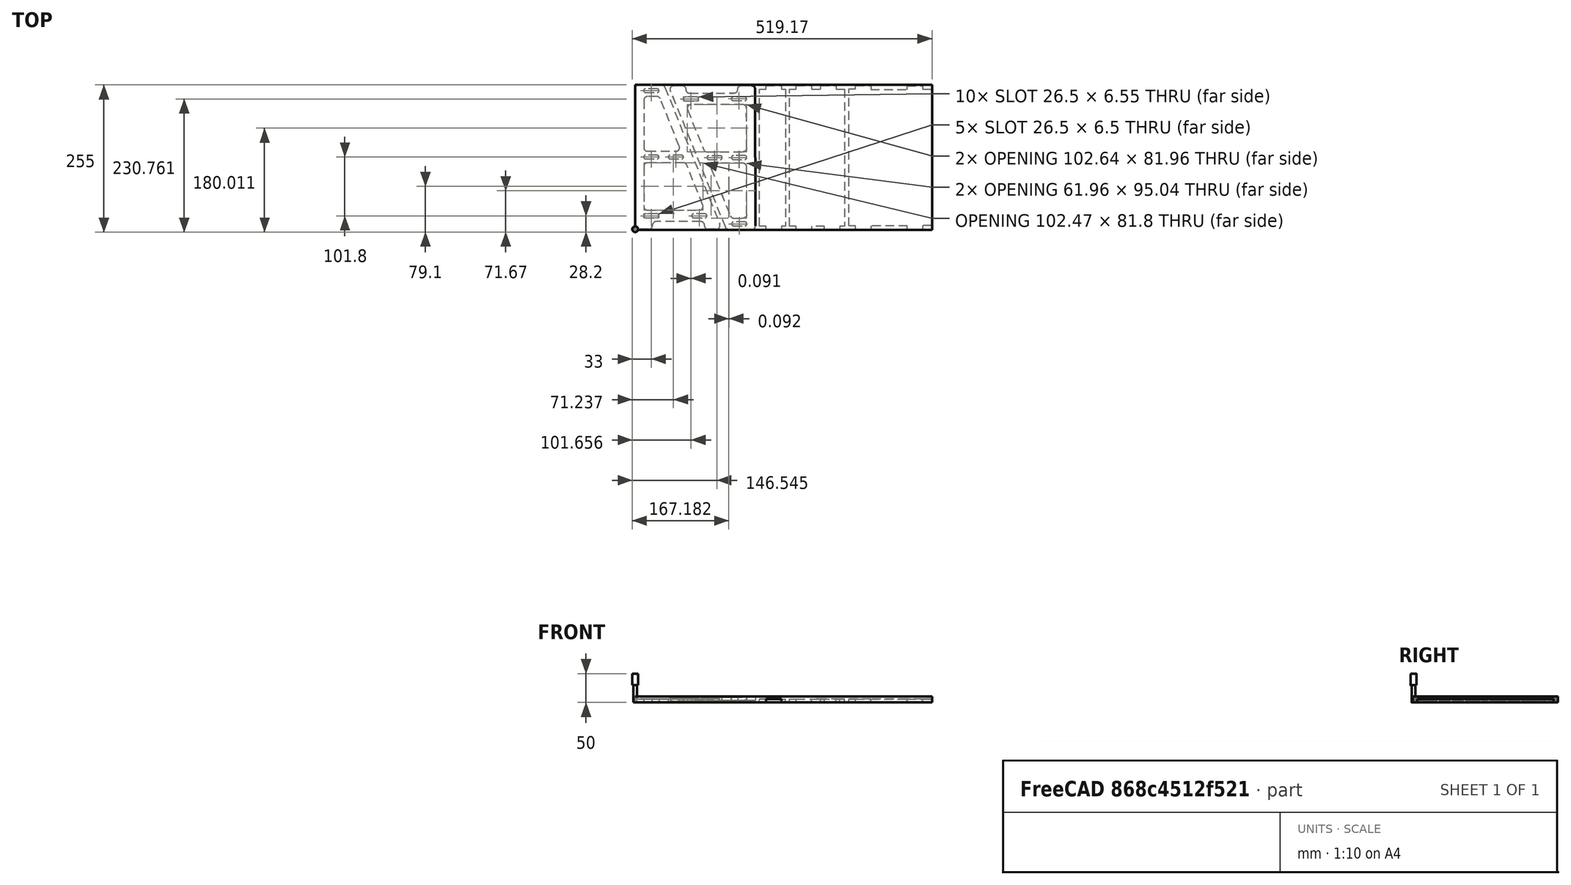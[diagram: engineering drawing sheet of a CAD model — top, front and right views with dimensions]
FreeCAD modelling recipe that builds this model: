
FCSTD DOCUMENT  (FreeCAD 0.19R14555 (Git shallow))
Label: Stand2
License: All rights reserved
LicenseURL: http://en.wikipedia.org/wiki/All_rights_reserved
objects: Part::FeaturePython×8, Sketcher::SketchObject×4, PartDesign::Pad×4, PartDesign::Body×4, Path::FeaturePython×4, App::DocumentObjectGroup×2, PartDesign::Fillet×1, App::FeaturePython×1, Spreadsheet::Sheet×1, Part::Mirroring×1, Path::FeatureCompoundPython×1, Mesh::FeaturePython×1
note: 29 computed .brp shape members not serialized (recipe doc carries the construction recipe); baked Part::Feature solids carry a one-line shape summary decoded from their .brp

FEATURE [Sketcher::SketchObject] Sketch
  FullyConstrained = true
  MapMode = 5
  Support = -> [XY_Plane]
  expr: Constraints[96] = <<Spreadsheet>>.TongueGapLower
  expr: Constraints[94] = <<Spreadsheet>>.SlotCentre
  expr: Constraints[83] = <<Spreadsheet>>.TongueToBack
  expr: Constraints[81] = <<Spreadsheet>>.Tool
  expr: Constraints[72] = <<Spreadsheet>>.TongueToBack
  expr: Constraints[91] = <<Spreadsheet>>.SlotSize
  expr: Constraints[92] = <<Spreadsheet>>.Tool
  expr: Constraints[71] = <<Spreadsheet>>.SlotSize
  expr: Constraints[67] = <<Spreadsheet>>.Tool
  expr: Constraints[53] = <<Spreadsheet>>.Tool
  expr: Constraints[68] = <<Spreadsheet>>.Tool
  expr: Constraints[82] = <<Spreadsheet>>.SlotSize
  expr: Constraints[52] = <<Spreadsheet>>.SlotSize
  expr: Constraints[27] = <<Spreadsheet>>.Top
  expr: Constraints[70] = <<Spreadsheet>>.SlotSize
  expr: Constraints[55] = <<Spreadsheet>>.TongueToBack
  expr: Constraints[29] = <<Spreadsheet>>.Bottom
  expr: Constraints[95] = <<Spreadsheet>>.TongueGapMid
  expr: Constraints[26] = <<Spreadsheet>>.Height
  sketch-geometry (36):
    g0: LineSegment StartX=0 StartY=250 StartZ=0 EndX=50 EndY=250 EndZ=0
    g1: LineSegment StartX=150 StartY=0 StartZ=0 EndX=120 EndY=0 EndZ=0
    g2: LineSegment StartX=0 StartY=0 StartZ=0 EndX=0 EndY=250 EndZ=0
    g3: LineSegment StartX=50 StartY=250 StartZ=0 EndX=150 EndY=0 EndZ=0
    g4: LineSegment StartX=15 StartY=230 StartZ=0 EndX=15 EndY=135 EndZ=0
    g5: LineSegment StartX=15 StartY=135 StartZ=0 EndX=79.8445 EndY=135 EndZ=0
    g6: LineSegment StartX=79.8445 StartY=135 StartZ=0 EndX=41.8445 EndY=230 EndZ=0
    g7: LineSegment StartX=41.8445 StartY=230 StartZ=0 EndX=15 EndY=230 EndZ=0
    g8: LineSegment StartX=15 StartY=115 StartZ=0 EndX=15 EndY=33.2 EndZ=0
    g9: LineSegment StartX=15 StartY=33.2 StartZ=0 EndX=120.565 EndY=33.2 EndZ=0
    g10: LineSegment StartX=120.565 StartY=33.2 StartZ=0 EndX=87.8445 EndY=115 EndZ=0
    g11: LineSegment StartX=87.8445 StartY=115 StartZ=0 EndX=15 EndY=115 EndZ=0
    g12: LineSegment StartX=120 StartY=0 StartZ=0 EndX=120 EndY=13.2 EndZ=0
    g13: LineSegment StartX=120 StartY=13.2 StartZ=0 EndX=30 EndY=13.2 EndZ=0
    g14: LineSegment StartX=30 StartY=13.2 StartZ=0 EndX=30 EndY=0 EndZ=0
    g15: LineSegment StartX=30 StartY=0 StartZ=0 EndX=0 EndY=0 EndZ=0
    g16: ArcOfCircle CenterX=18 CenterY=240 CenterZ=0 NormalX=0 NormalY=0 NormalZ=1 AngleXU=0 Radius=3.25 StartAngle=1.5708 EndAngle=4.71239
    g17: ArcOfCircle CenterX=38 CenterY=240 CenterZ=0 NormalX=0 NormalY=0 NormalZ=1 AngleXU=0 Radius=3.25 StartAngle=4.71239 EndAngle=7.85398
    g18: LineSegment StartX=18 StartY=236.75 StartZ=0 EndX=38 EndY=236.75 EndZ=0
    g19: LineSegment StartX=38 StartY=243.25 StartZ=0 EndX=18 EndY=243.25 EndZ=0
    g20: ArcOfCircle CenterX=60.5 CenterY=125 CenterZ=0 NormalX=0 NormalY=0 NormalZ=1 AngleXU=0 Radius=3.25 StartAngle=1.5708 EndAngle=4.71239
    g21: ArcOfCircle CenterX=80.5 CenterY=125 CenterZ=0 NormalX=0 NormalY=0 NormalZ=1 AngleXU=0 Radius=3.25 StartAngle=4.71239 EndAngle=7.85398
    g22: LineSegment StartX=60.5 StartY=121.75 StartZ=0 EndX=80.5 EndY=121.75 EndZ=0
    g23: LineSegment StartX=80.5 StartY=128.25 StartZ=0 EndX=60.5 EndY=128.25 EndZ=0
    g24: ArcOfCircle CenterX=18 CenterY=125 CenterZ=0 NormalX=0 NormalY=0 NormalZ=1 AngleXU=0 Radius=3.25 StartAngle=1.5708 EndAngle=4.71239
    g25: ArcOfCircle CenterX=38 CenterY=125 CenterZ=0 NormalX=0 NormalY=0 NormalZ=1 AngleXU=0 Radius=3.25 StartAngle=4.71239 EndAngle=7.85398
    g26: LineSegment StartX=18 StartY=121.75 StartZ=0 EndX=38 EndY=121.75 EndZ=0
    g27: LineSegment StartX=38 StartY=128.25 StartZ=0 EndX=18 EndY=128.25 EndZ=0
    g28: ArcOfCircle CenterX=18 CenterY=23.2 CenterZ=0 NormalX=0 NormalY=0 NormalZ=1 AngleXU=0 Radius=3.25 StartAngle=1.5708 EndAngle=4.71239
    g29: ArcOfCircle CenterX=38 CenterY=23.2 CenterZ=0 NormalX=0 NormalY=0 NormalZ=1 AngleXU=0 Radius=3.25 StartAngle=4.71239 EndAngle=7.85398
    g30: LineSegment StartX=18 StartY=19.95 StartZ=0 EndX=38 EndY=19.95 EndZ=0
    g31: LineSegment StartX=38 StartY=26.45 StartZ=0 EndX=18 EndY=26.45 EndZ=0
    g32: ArcOfCircle CenterX=101 CenterY=23.2 CenterZ=0 NormalX=0 NormalY=0 NormalZ=1 AngleXU=0 Radius=3.25 StartAngle=1.5708 EndAngle=4.71239
    g33: ArcOfCircle CenterX=121 CenterY=23.2 CenterZ=0 NormalX=0 NormalY=0 NormalZ=1 AngleXU=0 Radius=3.25 StartAngle=4.71239 EndAngle=7.85398
    g34: LineSegment StartX=101 StartY=19.95 StartZ=0 EndX=121 EndY=19.95 EndZ=0
    g35: LineSegment StartX=121 StartY=26.45 StartZ=0 EndX=101 EndY=26.45 EndZ=0
  constraints (97):
    c: Coincident(g15,g2)
    c: Coincident(g2,g0)
    c: Horizontal(g0)
    c: Horizontal(g1)
    c: Vertical(g2)
    c: Vertical(g4)
    c: Coincident(g4,g5)
    c: Horizontal(g5)
    c: Coincident(g5,g6)
    c: Coincident(g6,g7)
    c: Coincident(g7,g4)
    c: Vertical(g8)
    c: Coincident(g8,g9)
    c: Coincident(g9,g10)
    c: Coincident(g10,g11)
    c: Coincident(g11,g8)
    c: Horizontal(g11)
    c: Coincident(g12,g13)
    c: Coincident(g13,g14)
    c: Horizontal(g13)
    c: Vertical(g12)
    c: Vertical(g14)
    c: Coincident(g15,g-1)
    c: Coincident(g0,g3)
    c: Parallel(g3,g10)
    c: Parallel(g3,g6)
    c: DistanceY(g2,g2) = 250
    c: DistanceX(g0,g0) = 50
    c: Coincident(g3,g1)
    c: DistanceX(g2,g1) = 150
    c: DistanceX(g15,g15) = 30
    c: DistanceX(g1,g1) = 30
    c: Coincident(g12,g1)
    c: Parallel(g13,g9)
    c: Parallel(g5,g7)
    c: Coincident(g14,g15)
    c: DistanceY(g14,g13) = 13.2
    c: DistanceY(g13,g8) = 20
    c: DistanceY(g8,g4) = 20
    c: DistanceY(g4,g0) = 20
    c: DistanceX(g2,g8) = 15
    c: DistanceX(g2,g4) = 15
    c: Horizontal(g15)
    c: Distance(g5,g3) = 15
    c: Distance(g10,g3) = 15
    c: DistanceY(g1,g2) = 0
    c: Tangent(g16,g18) = -1.5708
    c: Tangent(g18,g17) = -1.5708
    c: Tangent(g17,g19) = -1.5708
    c: Tangent(g19,g16) = -1.5708
    c: Equal(g16,g17)
    c: Horizontal(g18)
    c: DistanceX(g16,g17) = 20
    c: Diameter(g17) = 6.5
    c: DistanceY(g4,g16) = 10
    c: DistanceX(g0,g16) = 18
    c: Tangent(g20,g22) = -1.5708
    c: Tangent(g22,g21) = -1.5708
    c: Tangent(g21,g23) = -1.5708
    c: Tangent(g23,g20) = -1.5708
    c: Equal(g20,g21)
    c: Horizontal(g22)
    c: Tangent(g24,g26) = -1.5708
    c: Tangent(g26,g25) = -1.5708
    c: Tangent(g25,g27) = -1.5708
    c: Tangent(g27,g24) = -1.5708
    c: Equal(g24,g25)
    c: Diameter(g21) = 6.5
    c: Diameter(g24) = 6.5
    c: Parallel(g27,g5)
    c: DistanceX(g20,g21) = 20
    c: DistanceX(g24,g25) = 20
    c: DistanceX(g2,g24) = 18
    c: DistanceY(g8,g24) = 10
    c: DistanceY(g10,g21) = 10
    c: Tangent(g28,g30) = -1.5708
    c: Tangent(g30,g29) = -1.5708
    c: Tangent(g29,g31) = -1.5708
    c: Tangent(g31,g28) = -1.5708
    c: Equal(g28,g29)
    c: Horizontal(g30)
    c: Diameter(g29) = 6.5
    c: DistanceX(g28,g29) = 20
    c: DistanceX(g2,g28) = 18
    c: DistanceY(g13,g28) = 10
    c: Tangent(g32,g34) = -1.5708
    c: Tangent(g34,g33) = -1.5708
    c: Tangent(g33,g35) = -1.5708
    c: Tangent(g35,g32) = -1.5708
    c: Equal(g32,g33)
    c: Horizontal(g34)
    c: DistanceX(g32,g33) = 20
    c: Diameter(g33) = 6.5
    c: DistanceY(g12,g33) = 10
    c: DistanceY(g2,g24) = 125
    c: DistanceX(g25,g20) = 22.5
    c: DistanceX(g29,g32) = 63
FEATURE [PartDesign::Pad] Pad
  Direction = (0,0,1)
  Length = 6.25
  Length2 = 100
  Profile = -> Sketch
  Type = 0
  expr: Length = <<Spreadsheet>>.Thickness
FEATURE [PartDesign::Fillet] Fillet
  Base = -> Pad [Edge20,Edge2,Edge1,Edge5,Edge8,Edge17,Edge44,Edge37,Edge32,Edge25,Edge38,Edge26,Edge29,Edge41,Edge14,Edge11]
  BaseFeature = -> Pad
  Radius = 6.4
  SupportTransform = false
FEATURE [PartDesign::Body] Body
  Group = -> [Sketch,Pad,Fillet]
  Origin = -> Origin
  Tip = -> Fillet
FEATURE [App::FeaturePython] SetupSheet  # Path/CAM operation (typed FeaturePython)
  ClearanceHeightExpression = OpStockZMax+SetupSheet.ClearanceHeightOffset
  ClearanceHeightOffset = 5
  CoolantMode = 0
  CoolantModes = None | Flood | Mist
  FinalDepthExpression = OpFinalDepth
  HorizRapid = 0
  SafeHeightExpression = OpStockZMax+SetupSheet.SafeHeightOffset
  SafeHeightOffset = 3
  StartDepthExpression = OpStartDepth
  StepDownExpression = OpToolDiameter
  VertRapid = 0
FEATURE [Part::FeaturePython] Clone  label="Model-Body"  # Draft clone (typed FeaturePython)
  AttacherType = Attacher::AttachEngine3D
  Fuse = false
  Objects = -> [Body]
  PathResource = Model
  Scale = (1,1,1)
FEATURE [Part::FeaturePython] ToolBit001  label="6.4mm Endmill"  # Path/CAM toolbit (typed FeaturePython)
  BitPropertyNames = Chipload | CuttingEdgeHeight | Diameter | Flutes | Length | Material | ShankDiameter
  BitShape = <path>
  Chipload = 0
  CuttingEdgeHeight = 30
  Diameter = 6.4
  File = <userpath>/MensShed/CNCRouter/FreeCAD/Bit/6.4mm_Endmill.fctb
  Flutes = 0
  Length = 50
  Material = 0
  ShankDiameter = 10
  ShapeName = endmill
FEATURE [Path::FeaturePython] __4mm_Endmill  label="6.4mm Endmill001"  # Path/CAM operation (typed FeaturePython)
  HorizFeed = 10
  HorizRapid = 0
  SpindleDir = 0
  SpindleSpeed = 10000
  Tool = -> ToolBit001
  ToolNumber = 2
  VertFeed = 10
  VertRapid = 0
  expr: VertRapid = SetupSheet.VertRapid
  expr: HorizRapid = SetupSheet.HorizRapid
FEATURE [App::DocumentObjectGroup] Tools
  Group = -> [__4mm_Endmill]
FEATURE [Spreadsheet::Sheet] Spreadsheet
  cells = A2=Material Thickness; B2(Thickness)=6.25; A3=Tool Size; B3(Tool)=6.5; A5=Height; B5(Height)=250; A6=Bottom Width; B6(Bottom)=150; A7=Top Width; B7(Top)=50; A8=SlotSize; B8(SlotSize)=20; A9=TongueSize; B9(TongueSize)==B8 + B3; A10=Tongue to back; B10(TongueToBack)=18; A11=Centre; B11(SlotCentre)==B5 / 2; A12=Mid Tongue Gap; B12(TongueGapMid)=22.5; A13=Lower Tongue Gap; B13(TongueGapLower)=63; A15=TopShelf; B15(ShelfTop)==B7 - 5; A16=MidShelf; B16(ShelfMid)==(B6 + B7) / 2 - 5; A17=Bottom Shelf; B17(ShelfBottom)==B6 - 6; A18=Shelf Width; B18(ShelfWidth)==B5 - B2 * 2
FEATURE [Part::Mirroring] mirror  label="Body (mirrored) "
  Base = (159.181,124.226,5.79083)
  Normal = (-0.999887,-0.00161748,0.0149187)
  Placement = pos=(-110.969,247.905,10.4582) rot=(0.999967,0.002919,-0.00759;3.14398rad)
  Source = -> Body
FEATURE [Path::FeaturePython] Profile001  label="Inside"  # Path/CAM operation (typed FeaturePython)
  Active = true
  AreaParams:
    Tolerance = 1e-07
    FitArcs = True
    Simplify = False
    CleanDistance = 0.0
    Accuracy = 0.01
    Unit = 1.0
    MinArcPoints = 4
    MaxArcPoints = 100
    ClipperScale = 10000000.0
    Fill = 0
    Coplanar = 0
    Reorient = True
    Outline = False
    Explode = False
    OpenMode = 0
    Deflection = 0.01
    SubjectFill = 0
    ClipFill = 0
    Offset = -3.2
    ExtraPass = 0
    Stepover = 0.0
    LastStepover = 0.0
    JoinType = 0
    EndType = 0
    MiterLimit = 2.0
    RoundPrecision = 0.0
    PocketMode = 0
    ToolRadius = 1.0
    PocketExtraOffset = 0.0
    PocketStepover = 0.0
    PocketLastStepover = 0.0
    FromCenter = False
    Angle = 45.0
    AngleShift = 0.0
    Shift = 0.0
    Thicken = False
    SectionCount = -1
    Stepdown = 1.0
    SectionOffset = 0.0
    SectionTolerance = 1e-06
    SectionMode = 2
    Project = False
  AttemptInverseAngle = true
  Base = -> [Clone,mirror]
  ClearanceHeight = 15.36
  CoolantMode = 0
  CycleTime = 00:09:32
  Direction = 0
  EnableRotation = 0
  FinalDepth = 0
  HandleMultipleFeatures = 0
  InverseAngle = false
  JoinType = 0
  LimitDepthToFace = true
  MiterLimit = 0.1
  OffsetExtra = 0
  OpFinalDepth = 10.0479
  OpStartDepth = 10.3617
  OpStockZMax = 10.36
  OpStockZMin = 0
  OpToolDiameter = 6.4
  PathParams = {'orientation': 1, 'feedrate': 10.0, 'feedrate_v': 10.0, 'verbose': True, 'resume_height': 13.36, 'retraction': 15.36, 'return_end': True, 'preamble': False, 'start': Vector (169.60857197117457, 225.95164355995647, 15.36)}
  ReverseDirection = false
  SafeHeight = 13.36
  Side = 1
  SplitArcs = false
  StartDepth = 6.25
  StartPoint = (0,0,0)
  StepDown = 3
  ToolController = -> __4mm_Endmill
  UseComp = true
  UseStartPoint = false
  processCircles = false
  processHoles = false
  processPerimeter = true
  expr: StepDown = 3
  expr: StartDepth = <<Spreadsheet>>.Thickness
  expr: SafeHeight = OpStockZMax + SetupSheet.SafeHeightOffset
  expr: FinalDepth = 0
  expr: ClearanceHeight = OpStockZMax + SetupSheet.ClearanceHeightOffset
FEATURE [Sketcher::SketchObject] Sketch001
  FullyConstrained = false
  MapMode = 5
  Support = -> [XY_Plane001]
  expr: Constraints[30] = <<Spreadsheet>>.TongueToBack - <<Spreadsheet>>.Tool
  expr: Constraints[9] = <<Spreadsheet>>.ShelfWidth
  expr: Constraints[27] = <<Spreadsheet>>.Thickness
  expr: Constraints[29] = <<Spreadsheet>>.TongueToBack - <<Spreadsheet>>.Tool
  expr: Constraints[26] = <<Spreadsheet>>.TongueSize
  expr: Constraints[8] = <<Spreadsheet>>.ShelfTop
  expr: Constraints[16] = <<Spreadsheet>>.Thickness
  expr: Constraints[15] = <<Spreadsheet>>.TongueSize
  sketch-geometry (13):
    g0: LineSegment StartX=222.075 StartY=243.75 StartZ=0 EndX=231.81 EndY=243.75 EndZ=0
    g1: LineSegment StartX=267.075 StartY=243.75 StartZ=0 EndX=267.075 EndY=6.25 EndZ=0
    g2: LineSegment StartX=267.075 StartY=6.25 StartZ=0 EndX=260.075 EndY=6.25 EndZ=0
    g3: LineSegment StartX=222.075 StartY=6.25 StartZ=0 EndX=222.075 EndY=243.75 EndZ=0
    g4: LineSegment StartX=260.075 StartY=6.25 StartZ=0 EndX=260.075 EndY=0 EndZ=0
    g5: LineSegment StartX=260.075 StartY=0 StartZ=0 EndX=233.575 EndY=0 EndZ=0
    g6: LineSegment StartX=233.575 StartY=0 StartZ=0 EndX=233.575 EndY=6.25 EndZ=0
    g7: LineSegment StartX=233.575 StartY=6.25 StartZ=0 EndX=222.075 EndY=6.25 EndZ=0
    g8: LineSegment StartX=233.575 StartY=250 StartZ=0 EndX=260.075 EndY=250 EndZ=0
    g9: LineSegment StartX=260.075 StartY=250 StartZ=0 EndX=260.075 EndY=243.75 EndZ=0
    g10: LineSegment StartX=231.81 StartY=243.75 StartZ=0 EndX=233.575 EndY=243.75 EndZ=0
    g11: LineSegment StartX=233.575 StartY=243.75 StartZ=0 EndX=233.575 EndY=250 EndZ=0
    g12: LineSegment StartX=260.075 StartY=243.75 StartZ=0 EndX=267.075 EndY=243.75 EndZ=0
  constraints (34):
    c: Coincident(g12,g1)
    c: Coincident(g1,g2)
    c: Coincident(g7,g3)
    c: Coincident(g3,g0)
    c: Horizontal(g0)
    c: Horizontal(g2)
    c: Vertical(g1)
    c: Vertical(g3)
    c: DistanceX(g0,g12) = 45
    c: DistanceY(g3,g3) = 237.5
    c: Coincident(g4,g5)
    c: Coincident(g5,g6)
    c: Horizontal(g5)
    c: Vertical(g4)
    c: Vertical(g6)
    c: DistanceX(g5,g5) = 26.5
    c: DistanceY(g4,g4) = 6.25
    c: DistanceY(g-1,g5) = 0
    c: Parallel(g5,g7)
    c: Coincident(g8,g9)
    c: Coincident(g10,g11)
    c: Coincident(g11,g8)
    c: Horizontal(g8)
    c: Horizontal(g10)
    c: Vertical(g9)
    c: Vertical(g11)
    c: DistanceX(g8,g8) = 26.5
    c: DistanceY(g9,g9) = 6.25
    c: PointOnObject(g10,g0)
    c: DistanceX(g0,g8) = 11.5
    c: DistanceX(g3,g5) = 11.5
    c: Coincident(g7,g6)
    c: Coincident(g12,g9)
    c: Coincident(g2,g4)
FEATURE [PartDesign::Pad] Pad001
  Direction = (0,0,1)
  Length = 6.25
  Length2 = 10
  Profile = -> Sketch001
  Type = 0
  expr: Length = <<Spreadsheet>>.Thickness
FEATURE [PartDesign::Body] Body001  label="TopShelf"
  Group = -> [Sketch001,Pad001]
  Origin = -> Origin001
  Placement = pos=(-7,-1,0) rot=(0,0,1;0rad)
  Tip = -> Pad001
FEATURE [Sketcher::SketchObject] Sketch002
  FullyConstrained = false
  MapMode = 5
  Support = -> [XY_Plane002]
  expr: Constraints[9] = <<Spreadsheet>>.ShelfMid
  expr: Constraints[55] = <<Spreadsheet>>.Thickness
  expr: Constraints[54] = <<Spreadsheet>>.Thickness
  expr: Constraints[56] = <<Spreadsheet>>.Thickness
  expr: Constraints[8] = <<Spreadsheet>>.ShelfWidth
  expr: Constraints[48] = <<Spreadsheet>>.Thickness
  expr: Constraints[47] = <<Spreadsheet>>.Thickness
  expr: Constraints[46] = <<Spreadsheet>>.Thickness
  expr: Constraints[42] = <<Spreadsheet>>.TongueGapMid
  expr: Constraints[37] = <<Spreadsheet>>.TongueToBack - <<Spreadsheet>>.Tool
  expr: Constraints[43] = <<Spreadsheet>>.TongueSize
  expr: Constraints[36] = <<Spreadsheet>>.TongueSize
  expr: Constraints[49] = <<Spreadsheet>>.Thickness
  expr: Constraints[33] = <<Spreadsheet>>.TongueSize
  expr: Constraints[38] = <<Spreadsheet>>.TongueSize
  expr: Constraints[32] = <<Spreadsheet>>.TongueGapMid - <<Spreadsheet>>.Tool
  expr: Constraints[31] = <<Spreadsheet>>.TongueToBack - <<Spreadsheet>>.Tool
  sketch-geometry (20):
    g0: LineSegment StartX=280.425 StartY=243.877 StartZ=0 EndX=291.925 EndY=243.877 EndZ=0
    g1: LineSegment StartX=375.425 StartY=243.877 StartZ=0 EndX=375.425 EndY=6.37686 EndZ=0
    g2: LineSegment StartX=375.425 StartY=6.37686 StartZ=0 EndX=367.425 EndY=6.37686 EndZ=0
    g3: LineSegment StartX=280.425 StartY=6.44568 StartZ=0 EndX=280.425 EndY=243.877 EndZ=0
    g4: LineSegment StartX=291.925 StartY=250.127 StartZ=0 EndX=318.425 EndY=250.127 EndZ=0
    g5: LineSegment StartX=318.425 StartY=250.127 StartZ=0 EndX=318.425 EndY=243.877 EndZ=0
    g6: LineSegment StartX=291.925 StartY=243.877 StartZ=0 EndX=291.925 EndY=250.127 EndZ=0
    g7: LineSegment StartX=334.425 StartY=250.127 StartZ=0 EndX=360.925 EndY=250.127 EndZ=0
    g8: LineSegment StartX=360.925 StartY=250.127 StartZ=0 EndX=360.925 EndY=243.877 EndZ=0
    g9: LineSegment StartX=334.425 StartY=243.877 StartZ=0 EndX=334.425 EndY=250.127 EndZ=0
    g10: LineSegment StartX=318.425 StartY=6.37686 StartZ=0 EndX=318.425 EndY=0.195678 EndZ=0
    g11: LineSegment StartX=318.425 StartY=0.195678 StartZ=0 EndX=291.925 EndY=0.195678 EndZ=0
    g12: LineSegment StartX=291.925 StartY=0.195678 StartZ=0 EndX=291.925 EndY=6.44568 EndZ=0
    g13: LineSegment StartX=367.425 StartY=6.37686 StartZ=0 EndX=367.425 EndY=0.126858 EndZ=0
    g14: LineSegment StartX=367.425 StartY=0.126858 StartZ=0 EndX=340.925 EndY=0.126858 EndZ=0
    g15: LineSegment StartX=340.925 StartY=0.126858 StartZ=0 EndX=340.925 EndY=6.37686 EndZ=0
    g16: LineSegment StartX=318.425 StartY=243.877 StartZ=0 EndX=334.425 EndY=243.877 EndZ=0
    g17: LineSegment StartX=360.925 StartY=243.877 StartZ=0 EndX=375.425 EndY=243.877 EndZ=0
    g18: LineSegment StartX=291.925 StartY=6.44568 StartZ=0 EndX=280.425 EndY=6.44568 EndZ=0
    g19: LineSegment StartX=340.925 StartY=6.37686 StartZ=0 EndX=318.425 EndY=6.37686 EndZ=0
  constraints (57):
    c: Coincident(g17,g1)
    c: Coincident(g1,g2)
    c: Coincident(g18,g3)
    c: Coincident(g3,g0)
    c: Horizontal(g0)
    c: Horizontal(g2)
    c: Vertical(g1)
    c: Vertical(g3)
    c: DistanceY(g1,g1) = 237.5
    c: DistanceX(g0,g17) = 95
    c: Coincident(g4,g5)
    c: Coincident(g6,g4)
    c: Horizontal(g4)
    c: Vertical(g5)
    c: Vertical(g6)
    c: Coincident(g7,g8)
    c: Coincident(g9,g7)
    c: Horizontal(g7)
    c: Vertical(g8)
    c: Vertical(g9)
    c: PointOnObject(g8,g0)
    c: Coincident(g10,g11)
    c: Coincident(g11,g12)
    c: Horizontal(g11)
    c: Vertical(g10)
    c: Vertical(g12)
    c: Coincident(g13,g14)
    c: Coincident(g14,g15)
    c: Horizontal(g14)
    c: Vertical(g13)
    c: Vertical(g15)
    c: DistanceX(g0,g4) = 11.5
    c: DistanceX(g4,g7) = 16
    c: DistanceX(g4,g4) = 26.5
    c: Coincident(g16,g5)
    c: PointOnObject(g16,g9)
    c: DistanceX(g7,g7) = 26.5
    c: DistanceX(g3,g11) = 11.5
    c: DistanceX(g11,g11) = 26.5
    c: Coincident(g18,g12)
    c: Coincident(g10,g19)
    c: Coincident(g19,g15)
    c: DistanceX(g19,g19) = 22.5
    c: DistanceX(g14,g14) = 26.5
    c: Coincident(g0,g6)
    c: Coincident(g17,g8)
    c: DistanceY(g1,g7) = 6.25
    c: DistanceY(g9,g9) = 6.25
    c: DistanceY(g5,g5) = 6.25
    c: DistanceY(g6,g6) = 6.25
    c: Parallel(g16,g4)
    c: Parallel(g18,g11)
    c: Parallel(g19,g11)
    c: Coincident(g2,g13)
    c: DistanceY(g12,g12) = 6.25
    c: DistanceY(g15,g15) = 6.25
    c: DistanceY(g13,g13) = 6.25
FEATURE [PartDesign::Pad] Pad002
  Direction = (0,0,1)
  Length = 6.25
  Length2 = 10
  Profile = -> Sketch002
  Type = 0
  expr: Length = <<Spreadsheet>>.Thickness
FEATURE [PartDesign::Body] Body002  label="MidShelf"
  Group = -> [Sketch002,Pad002]
  Origin = -> Origin002
  Placement = pos=(-13,-1,0) rot=(0,0,1;0rad)
  Tip = -> Pad002
FEATURE [Sketcher::SketchObject] Sketch003
  FullyConstrained = false
  MapMode = 5
  Support = -> [XY_Plane003]
  expr: Constraints[54] = <<Spreadsheet>>.TongueToBack - <<Spreadsheet>>.Thickness
  expr: Constraints[53] = <<Spreadsheet>>.TongueGapLower
  expr: Constraints[51] = <<Spreadsheet>>.TongueSize
  expr: Constraints[4] = <<Spreadsheet>>.ShelfBottom
  expr: Constraints[46] = <<Spreadsheet>>.Thickness
  expr: Constraints[49] = <<Spreadsheet>>.Thickness
  expr: Constraints[45] = <<Spreadsheet>>.Thickness
  expr: Constraints[52] = <<Spreadsheet>>.TongueSize
  expr: Constraints[48] = <<Spreadsheet>>.ShelfWidth
  expr: Constraints[44] = <<Spreadsheet>>.Thickness
  expr: Constraints[37] = <<Spreadsheet>>.TongueToBack - <<Spreadsheet>>.Tool
  expr: Constraints[35] = <<Spreadsheet>>.TongueSize
  expr: Constraints[50] = <<Spreadsheet>>.Thickness
  expr: Constraints[36] = <<Spreadsheet>>.TongueGapLower
  expr: Constraints[34] = <<Spreadsheet>>.TongueSize
  sketch-geometry (20):
    g0: LineSegment StartX=533.172 StartY=242.596 StartZ=0 EndX=533.172 EndY=6.51215 EndZ=0
    g1: LineSegment StartX=533.172 StartY=6.51215 StartZ=0 EndX=516.922 EndY=6.51215 EndZ=0
    g2: LineSegment StartX=389.172 StartY=5.54234 StartZ=0 EndX=389.172 EndY=243.042 EndZ=0
    g3: LineSegment StartX=400.672 StartY=249.292 StartZ=0 EndX=427.172 EndY=249.292 EndZ=0
    g4: LineSegment StartX=427.172 StartY=249.292 StartZ=0 EndX=427.172 EndY=242.267 EndZ=0
    g5: LineSegment StartX=400.672 StartY=243.042 StartZ=0 EndX=400.672 EndY=249.292 EndZ=0
    g6: LineSegment StartX=490.172 StartY=248.517 StartZ=0 EndX=516.672 EndY=248.517 EndZ=0
    g7: LineSegment StartX=516.672 StartY=248.517 StartZ=0 EndX=516.672 EndY=242.596 EndZ=0
    g8: LineSegment StartX=490.172 StartY=242.267 StartZ=0 EndX=490.172 EndY=248.517 EndZ=0
    g9: LineSegment StartX=427.422 StartY=5.54234 StartZ=0 EndX=427.422 EndY=-0.707665 EndZ=0
    g10: LineSegment StartX=427.422 StartY=-0.707665 StartZ=0 EndX=400.922 EndY=-0.707665 EndZ=0
    g11: LineSegment StartX=400.922 StartY=-0.707665 StartZ=0 EndX=400.922 EndY=5.54234 EndZ=0
    g12: LineSegment StartX=516.922 StartY=6.51215 StartZ=0 EndX=516.922 EndY=-0.707665 EndZ=0
    g13: LineSegment StartX=516.922 StartY=-0.707665 StartZ=0 EndX=490.422 EndY=-0.707665 EndZ=0
    g14: LineSegment StartX=490.422 StartY=-0.707665 StartZ=0 EndX=490.422 EndY=5.54234 EndZ=0
    g15: LineSegment StartX=389.172 StartY=243.042 StartZ=0 EndX=400.672 EndY=243.042 EndZ=0
    g16: LineSegment StartX=427.172 StartY=242.267 StartZ=0 EndX=490.172 EndY=242.267 EndZ=0
    g17: LineSegment StartX=516.672 StartY=242.596 StartZ=0 EndX=533.172 EndY=242.596 EndZ=0
    g18: LineSegment StartX=400.922 StartY=5.54234 StartZ=0 EndX=389.172 EndY=5.54234 EndZ=0
    g19: LineSegment StartX=490.422 StartY=5.54234 StartZ=0 EndX=427.422 EndY=5.54234 EndZ=0
  constraints (55):
    c: Coincident(g0,g1)
    c: Coincident(g18,g2)
    c: Horizontal(g1)
    c: Vertical(g0)
    c: DistanceX(g2,g0) = 144
    c: Coincident(g3,g4)
    c: Coincident(g5,g3)
    c: Horizontal(g3)
    c: Vertical(g4)
    c: Vertical(g5)
    c: Coincident(g6,g7)
    c: Coincident(g8,g6)
    c: Horizontal(g6)
    c: Vertical(g7)
    c: Vertical(g8)
    c: Coincident(g9,g10)
    c: Coincident(g10,g11)
    c: Horizontal(g10)
    c: Vertical(g9)
    c: Vertical(g11)
    c: Coincident(g12,g13)
    c: Coincident(g13,g14)
    c: Horizontal(g13)
    c: Vertical(g12)
    c: Vertical(g14)
    c: Horizontal(g17)
    c: Coincident(g7,g17)
    c: Coincident(g17,g0)
    c: Coincident(g8,g16)
    c: Coincident(g16,g4)
    c: Coincident(g15,g5)
    c: Coincident(g2,g15)
    c: Parallel(g15,g3)
    c: Parallel(g16,g3)
    c: DistanceX(g3,g3) = 26.5
    c: DistanceX(g6,g6) = 26.5
    c: DistanceX(g3,g6) = 63
    c: DistanceX(g2,g3) = 11.5
    c: Coincident(g18,g11)
    c: Coincident(g9,g19)
    c: Coincident(g19,g14)
    c: Coincident(g12,g1)
    c: Parallel(g18,g10)
    c: Parallel(g10,g19)
    c: DistanceY(g11,g11) = 6.25
    c: DistanceY(g9,g9) = 6.25
    c: DistanceY(g14,g14) = 6.25
    c: Perpendicular(g18,g2)
    c: DistanceY(g2,g2) = 237.5
    c: DistanceY(g5,g5) = 6.25
    c: DistanceY(g8,g8) = 6.25
    c: DistanceX(g10,g10) = 26.5
    c: DistanceX(g13,g13) = 26.5
    c: DistanceX(g19,g19) = 63
    c: DistanceX(g18,g18) = 11.75
FEATURE [PartDesign::Pad] Pad003
  Direction = (0,0,1)
  Length = 6.25
  Length2 = 10
  Profile = -> Sketch003
  Type = 0
  expr: Length = <<Spreadsheet>>.Thickness
FEATURE [PartDesign::Body] Body003  label="BottomShelf"
  Group = -> [Sketch003,Pad003]
  Origin = -> Origin003
  Placement = pos=(-19,0,0) rot=(0,0,1;0rad)
  Tip = -> Pad003
FEATURE [Path::FeaturePython] Profile  label="Outside"  # Path/CAM operation (typed FeaturePython)
  Active = true
  AreaParams:
    Tolerance = 1e-07
    FitArcs = True
    Simplify = False
    CleanDistance = 0.0
    Accuracy = 0.01
    Unit = 1.0
    MinArcPoints = 4
    MaxArcPoints = 100
    ClipperScale = 10000000.0
    Fill = 0
    Coplanar = 0
    Reorient = True
    Outline = False
    Explode = False
    OpenMode = 0
    Deflection = 0.01
    SubjectFill = 0
    ClipFill = 0
    Offset = 3.2
    ExtraPass = 0
    Stepover = 0.0
    LastStepover = 0.0
    JoinType = 0
    EndType = 0
    MiterLimit = 2.0
    RoundPrecision = 0.0
    PocketMode = 0
    ToolRadius = 1.0
    PocketExtraOffset = 0.0
    PocketStepover = 0.0
    PocketLastStepover = 0.0
    FromCenter = False
    Angle = 45.0
    AngleShift = 0.0
    Shift = 0.0
    Thicken = False
    SectionCount = -1
    Stepdown = 1.0
    SectionOffset = 0.0
    SectionTolerance = 1e-06
    SectionMode = 2
    Project = False
  AttemptInverseAngle = true
  Base = -> [mirror,Body001,Body002,Body003,Clone]
  ClearanceHeight = 15.36
  CoolantMode = 0
  CycleTime = 00:18:37
  Direction = 0
  EnableRotation = 0
  FinalDepth = 0
  HandleMultipleFeatures = 0
  InverseAngle = false
  JoinType = 0
  LimitDepthToFace = true
  MiterLimit = 0.1
  OffsetExtra = 0
  OpFinalDepth = 10.2824
  OpStartDepth = 10.3617
  OpStockZMax = 10.36
  OpStockZMin = 0
  OpToolDiameter = 6.4
  PathParams = {'orientation': 1, 'feedrate': 10.0, 'feedrate_v': 10.0, 'verbose': True, 'resume_height': 13.36, 'retraction': 15.36, 'return_end': True, 'preamble': False, 'start': Vector (264.2252453739803, 219.52913772072915, 15.36)}
  ReverseDirection = false
  SafeHeight = 13.36
  Side = 0
  SplitArcs = false
  StartDepth = 6.25
  StartPoint = (0,0,0)
  StepDown = 3
  ToolController = -> __4mm_Endmill
  UseComp = true
  UseStartPoint = false
  processCircles = false
  processHoles = false
  processPerimeter = true
  expr: StepDown = 3
  expr: StartDepth = <<Spreadsheet>>.Thickness
  expr: SafeHeight = OpStockZMax + SetupSheet.SafeHeightOffset
  expr: FinalDepth = 0
  expr: ClearanceHeight = OpStockZMax + SetupSheet.ClearanceHeightOffset
FEATURE [Path::FeatureCompoundPython] Operations  # Path/CAM operation (typed FeaturePython)
  Group = -> [Profile,Profile001]
  UsePlacements = false
FEATURE [Part::FeaturePython] Clone001  label="Model-Body (mirrored) "  # Draft clone (typed FeaturePython)
  AttacherType = Attacher::AttachEngine3D
  Fuse = false
  Objects = -> [mirror]
  PathResource = Model
  Placement = pos=(-110.969,247.905,10.4582) rot=(0.999967,0.002919,-0.00759;3.14398rad)
  Scale = (1,1,1)
FEATURE [Part::FeaturePython] Clone002  label="Model-BottomShelf"  # Draft clone (typed FeaturePython)
  AttacherType = Attacher::AttachEngine3D
  Fuse = false
  Objects = -> [Body003]
  PathResource = Model
  Placement = pos=(-19,0,0) rot=(0,0,1;0rad)
  Scale = (1,1,1)
FEATURE [Part::FeaturePython] Clone003  label="Model-MidShelf"  # Draft clone (typed FeaturePython)
  AttacherType = Attacher::AttachEngine3D
  Fuse = false
  Objects = -> [Body002]
  PathResource = Model
  Placement = pos=(-13,-1,0) rot=(0,0,1;0rad)
  Scale = (1,1,1)
FEATURE [Part::FeaturePython] Clone005  label="Model-TopShelf"  # Draft clone (typed FeaturePython)
  AttacherType = Attacher::AttachEngine3D
  Fuse = false
  Objects = -> [Body001]
  PathResource = Model
  Placement = pos=(-7,-1,0) rot=(0,0,1;0rad)
  Scale = (1,1,1)
FEATURE [Part::FeaturePython] Stock001  # WARN: FeaturePython — macro-defined, semantics opaque (R4)
  Height = 10.36
  Length = 514.17
  Placement = pos=(-1e-15,-1,0) rot=(0,0,1;0rad)
  StockType = CreateBox
  Width = 251
FEATURE [Mesh::FeaturePython] CutMaterial  # WARN: FeaturePython — macro-defined, semantics opaque (R4)
FEATURE [Path::FeaturePython] Job  # Path/CAM operation (typed FeaturePython)
  CycleTime = 00:28:09
  Fixtures = G54
  GeometryTolerance = 0.01
  JobType = 0
  LastPostProcessDate = 2022-02-14 14:27:24.473546
  LastPostProcessOutput = <userpath>/MensShed/CNCRouter/Shapes/Stand2
  Model = -> Model
  Operations = -> Operations
  OrderOutputBy = 0
  PostProcessor = 7
  PostProcessorOutputFile = %D/%d.ngc
  SetupSheet = -> SetupSheet
  SplitOutput = false
  Stock = -> Stock001
  Tools = -> Tools
FEATURE [App::DocumentObjectGroup] Model
  Group = -> [Clone,Clone001,Clone002,Clone003,Clone004,Clone005]
FEATURE [Part::FeaturePython] Clone004  label="Model-Model"  # Draft clone (typed FeaturePython)
  AttacherType = Attacher::AttachEngine3D
  Fuse = false
  Objects = -> [Model]
  PathResource = Model
  Scale = (1,1,1)
note: 1 file-system path scrubbed to <path> (originals preserved in the JSON sidecar)
